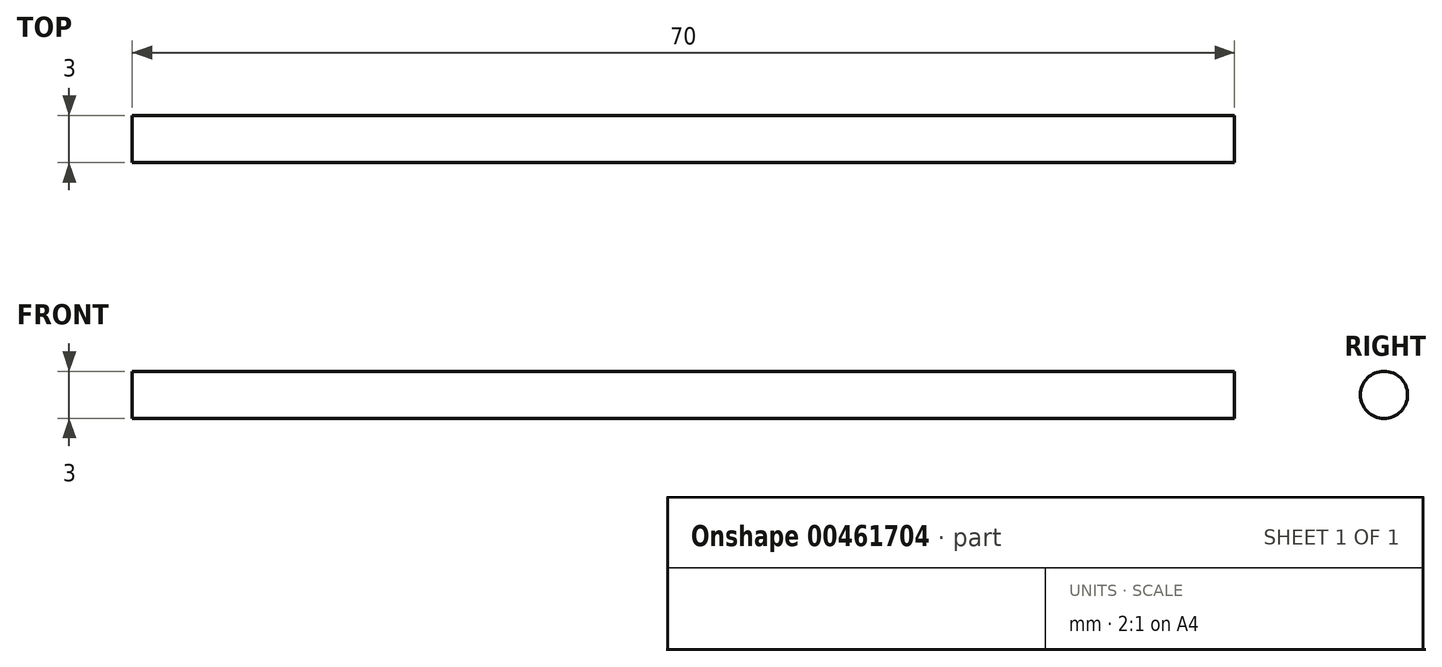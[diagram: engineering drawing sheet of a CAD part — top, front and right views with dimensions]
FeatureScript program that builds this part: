
annotation { "Feature Type Name" : "Feature", "Feature Type Description" : "" }
export const myFeature = defineFeature(function(context is Context, id is Id, definition is map)
    precondition{}
    {
        {
            var Q0;
            Q0=qCreatedBy(makeId("Right.planeOp"),FACE);
            var sketch = newSketch(context, id + "F0", { "sketchPlane" : qUnion([Q0])});
            skCircle(sketch, "E0", {"center": v(0, 0) * mm, "radius": 1.5 * mm});
            skSolve(sketch);
        }
        {
            var Q0;
            Q0=makeQuery(id+"F0.imprint","IMPRINT",FACE,{"disambiguationData":[TD([[makeQuery(id+"F0.imprint","IMPRINT",EDGE,{"derivedFrom":sQuery(id+"F0.wireOp",EDGE,"E0")}),1.0]])]});
            extrude(context, id + "F1", {"entities" : qUnion([Q0]), "endBound" : BoundingType.SYMMETRIC, "depth" : 70 * mm});
        }
    });
